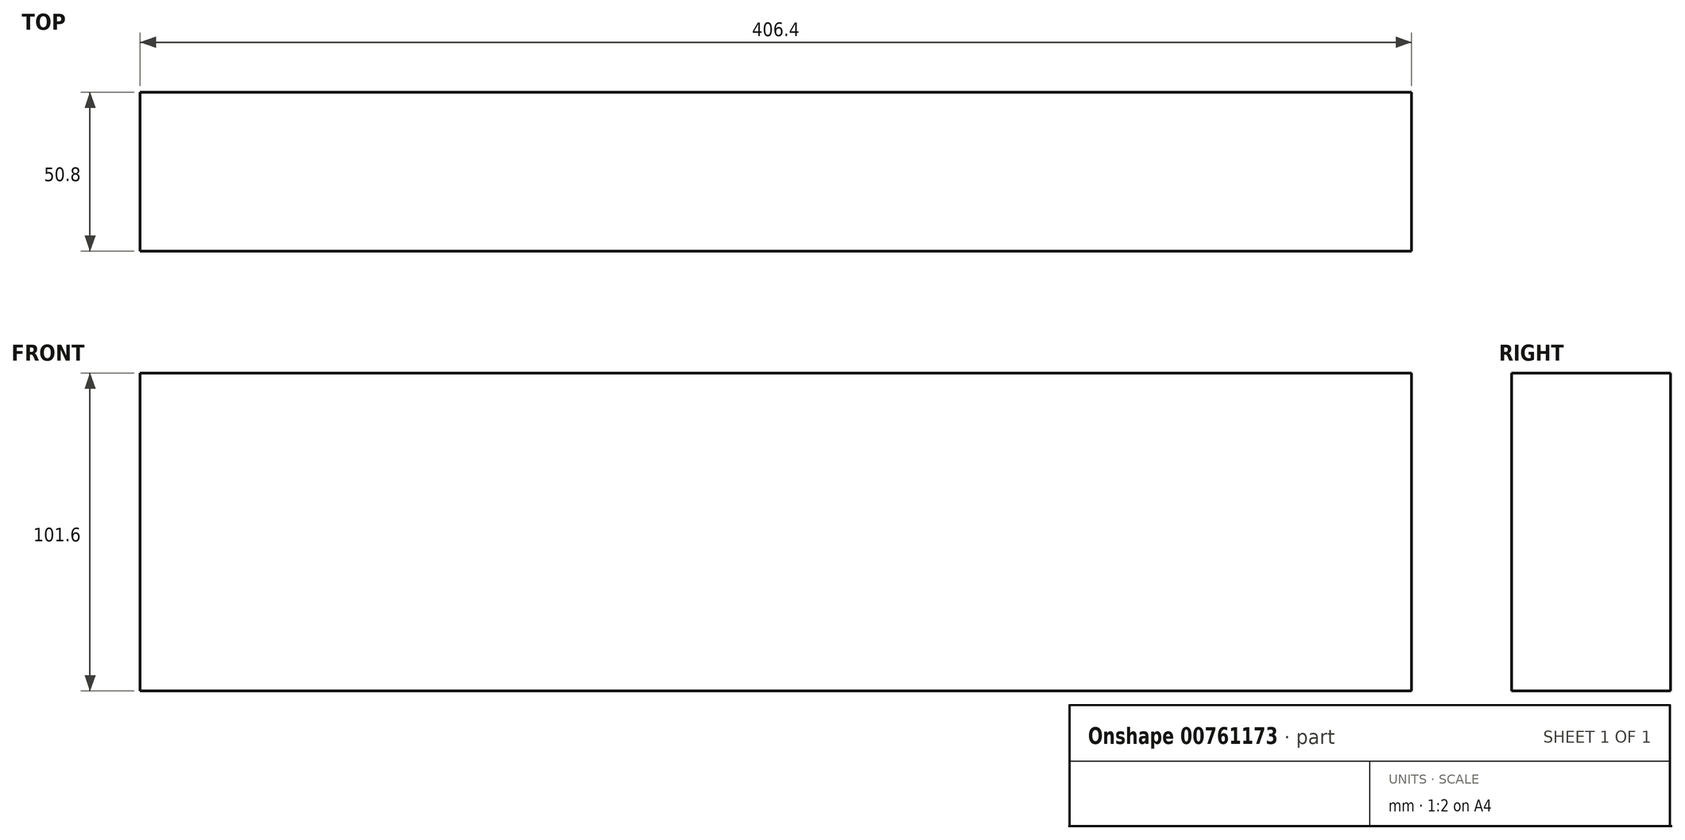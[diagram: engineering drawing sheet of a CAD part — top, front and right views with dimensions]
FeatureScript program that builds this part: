
annotation { "Feature Type Name" : "Feature", "Feature Type Description" : "" }
export const myFeature = defineFeature(function(context is Context, id is Id, definition is map)
    precondition{}
    {
        {
            var Q0;
            Q0=qCreatedBy(makeId("Front.planeOp"),FACE);
            var sketch = newSketch(context, id + "F0", { "sketchPlane" : qUnion([Q0])});
            skLineSegment(sketch, "E0.bottom", {"start": v(-65.16, 64.2) * mm, "end": v(341.24, 64.2) * mm});
            skLineSegment(sketch, "E0.top", {"start": v(-65.16, -37.4) * mm, "end": v(341.24, -37.4) * mm});
            skLineSegment(sketch, "E0.left", {"start": v(-65.16, 64.2) * mm, "end": v(-65.16, -37.4) * mm});
            skLineSegment(sketch, "E0.right", {"start": v(341.24, 64.2) * mm, "end": v(341.24, -37.4) * mm});
            skSolve(sketch);
        }
        {
            var Q0;
            Q0=makeQuery(id+"F0.imprint","IMPRINT",FACE,{"disambiguationData":[TD([[makeQuery(id+"F0.imprint","IMPRINT",EDGE,{"derivedFrom":sQuery(id+"F0.wireOp",EDGE,"E0.bottom")}),-1.0]])]});
            extrude(context, id + "F1", {"entities" : qUnion([Q0]), "depth" : 50.8 * mm, "offsetDistance" : 25.4 * mm});
        }
    });
